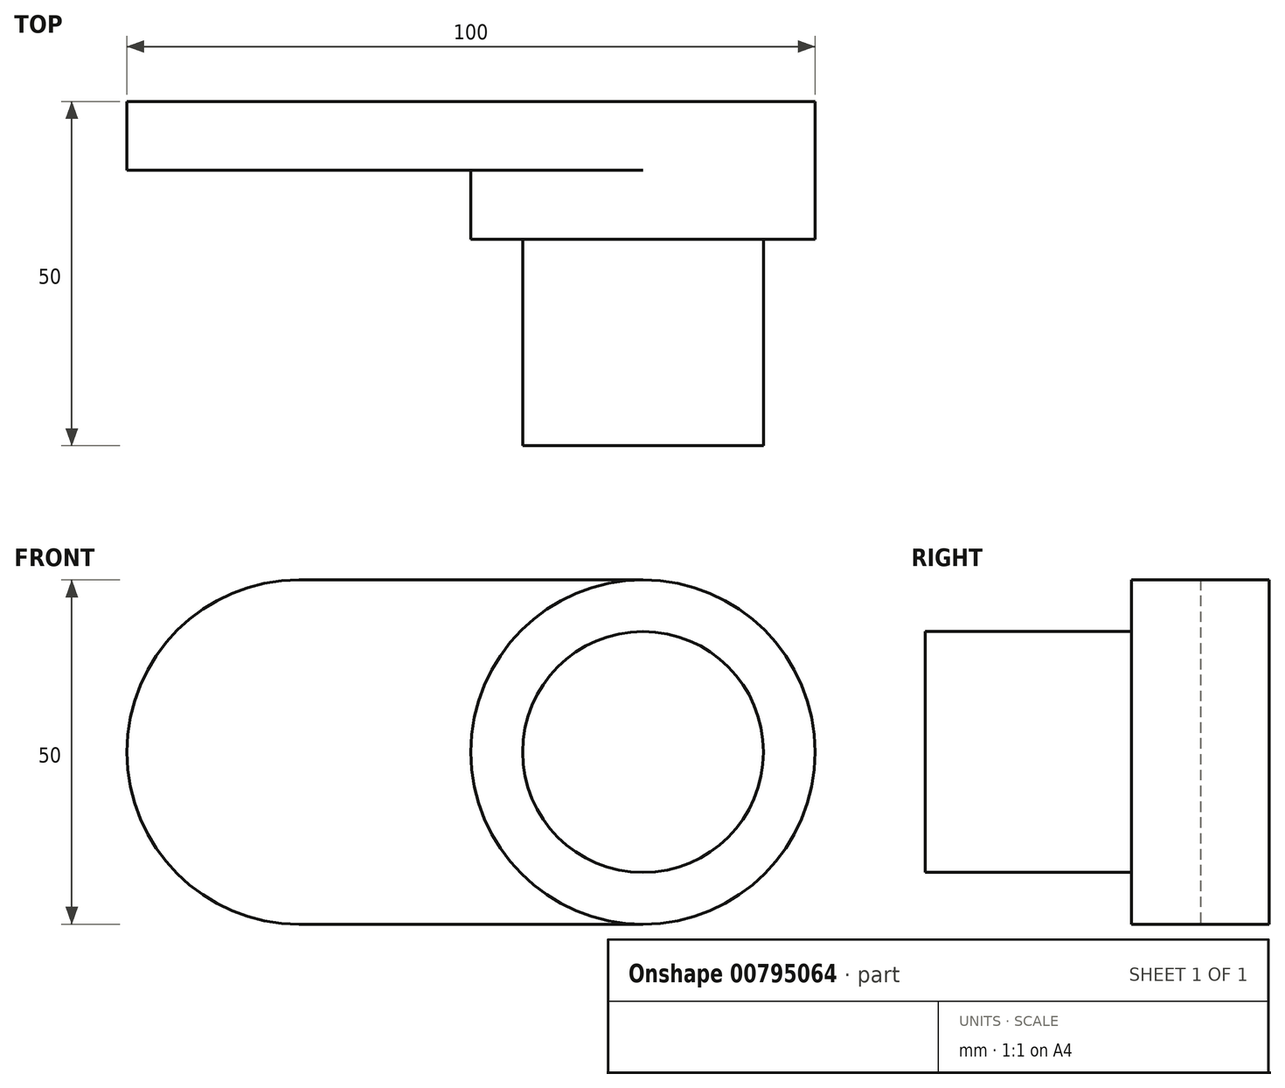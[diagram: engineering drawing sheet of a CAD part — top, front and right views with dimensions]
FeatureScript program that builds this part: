
annotation { "Feature Type Name" : "Feature", "Feature Type Description" : "" }
export const myFeature = defineFeature(function(context is Context, id is Id, definition is map)
    precondition{}
    {
        {
            var Q0;
            Q0=qCreatedBy(makeId("Front.planeOp"),FACE);
            var sketch = newSketch(context, id + "F0", { "sketchPlane" : qUnion([Q0])});
            skLineSegment(sketch, "E0.bottom", {"start": v(-22.48, 20.87) * mm, "end": v(27.52, 20.87) * mm});
            skLineSegment(sketch, "E0.top", {"start": v(-22.48, -29.13) * mm, "end": v(27.52, -29.13) * mm});
            skLineSegment(sketch, "E0.left", {"start": v(-47.48, -4.13) * mm, "end": v(-47.48, -4.13) * mm});
            skLineSegment(sketch, "E0.right", {"start": v(52.52, -4.13) * mm, "end": v(52.52, -4.13) * mm});
            skPoint(sketch, "E1.visualSharp", {"position": v(-47.48, 20.87) * mm});
            skArc(sketch, "E1.filletArc", {"start": v(-22.48, 20.87) * mm, "mid": v(-40.16, 13.55) * mm, "end": v(-47.48, -4.13) * mm});
            skPoint(sketch, "E2.visualSharp", {"position": v(-47.48, -29.13) * mm});
            skArc(sketch, "E2.filletArc", {"start": v(-47.48, -4.13) * mm, "mid": v(-40.16, -21.8) * mm, "end": v(-22.48, -29.13) * mm});
            skPoint(sketch, "E3.visualSharp", {"position": v(52.52, -29.13) * mm});
            skArc(sketch, "E3.filletArc", {"start": v(27.52, -29.13) * mm, "mid": v(45.2, -21.8) * mm, "end": v(52.52, -4.13) * mm});
            skPoint(sketch, "E4.visualSharp", {"position": v(52.52, 20.87) * mm});
            skArc(sketch, "E4.filletArc", {"start": v(52.52, -4.13) * mm, "mid": v(45.2, 13.55) * mm, "end": v(27.52, 20.87) * mm});
            skCircle(sketch, "E5", {"center": v(27.52, -4.13) * mm, "radius": 25 * mm});
            skCircle(sketch, "E6", {"center": v(27.52, -4.13) * mm, "radius": 17.5 * mm});
            skSolve(sketch);
        }
        {
            var Q0;
            {var subQ1=sQuery(id+"F0.wireOp",EDGE,"E0.bottom");Q0=makeQuery(id+"F0.imprint","IMPRINT",FACE,{"disambiguationData":[TD([[makeQuery(id+"F0.imprint","IMPRINT",EDGE,{"derivedFrom":subQ1}),-1.0]])]});}
            extrude(context, id + "F1", {"entities" : qUnion([Q0]), "depth" : 10 * mm, "offsetDistance" : 25 * mm});
        }
        {
            var Q0;
            Q0=makeQuery(id+"F0.imprint","IMPRINT",FACE,{"disambiguationData":[TD([[makeQuery(id+"F0.imprint","IMPRINT",EDGE,{"derivedFrom":sQuery(id+"F0.wireOp",EDGE,"E6")}),1.0]])]});
            extrude(context, id + "F2", {"entities" : qUnion([Q0]), "operationType" : NewBodyOperationType.ADD, "depth" : 50 * mm, "offsetDistance" : 25 * mm});
        }
        {
            var Q0;
            Q0=makeQuery(id+"F0.imprint","IMPRINT",FACE,{"disambiguationData":[TD([[makeQuery(id+"F0.imprint","IMPRINT",EDGE,{"derivedFrom":sQuery(id+"F0.wireOp",EDGE,"E6")}),-1.0]])]});
            extrude(context, id + "F3", {"entities" : qUnion([Q0]), "operationType" : NewBodyOperationType.ADD, "depth" : 20 * mm, "offsetDistance" : 25 * mm});
        }
    });
